# Revit family: Fireplace-Gas-Regency-Grandview_800EC
name_source: partatom
category: Mechanical Equipment
units: mm (PartAtom-declared; Revit-internal decimal feet)

## family parameters
Classification Number = 23.40.20.34.14
Cut with Voids When Loaded = Yes
Host = Face
Maintain Annotation Orientation = No
Part Type = Normal
Room Calculation Point = No
Round Connector Dimension = Use Diameter
Shared = No

## types (6) — shared parameters
Apparent Load = 0 VA
Assembly Code = D3020
C Connector Depth = 1' - 7 1/2"
C Opening Height = 2' - 7 9/16"
C Opening Width = 3' - 5"
Default Elevation = 0' - 0"
Depth = 1' - 6 7/8"
Description = G800EC Gas Fireplace
Exhaust Air Connection Diameter = 4"
Finish = Metal - Regency - Steel - Paint, Black Metallic
Frequency = 0 Hz
Glass Viewing Height = 2' - 10"
Glass Viewing Width = 3' - 0"
Height = 3' - 0 3/8"
Installation and Service URL = https://www.regency-fire.com
Keynote = 10300
Manufacturer = Regency Fireplace Products
Manufacturer Fax Number = 604-946-4349
Material = Painted Stainless Steel
Number of Poles = 1
Performance URL = https://www.regency-fire.com
Phase = 1
Product Documentation Link = https://assets.regency-fire.com
Product Name = Regency® Grandview™ G800EC Gas Fireplace
Product Page URL = https://www.regency-fire.com
Product Size = Medium
Room Size = Medium
Supply Air Connection Diameter = 7"
URL = https://www.regency-fire.com
Version = 2018 - v1.0a
Video Link = https://www.youtube.com
Voltage = 0 V
Warranty URL = https://www.regency-fire.com
Width = 2' - 11 7/8"
zero-valued in all types: Power Factor

## per-type parameters (varying)
| type | Constraints | Efficiency | EnerGuide Rating | Maximum BTU | Minimum BTU | Model |
| Cool Wall - LP | 1 | 68.16% | 57.74% | 25500.0 Btu/h | 21000.0 Btu/h | G800EC-LP |
| Clean Front - LP | 2 | 68.16% | 57.74% | 25500.0 Btu/h | 21000.0 Btu/h | G800EC-LP |
| Outside Finish - LP | 3 | 68.16% | 57.74% | 25500.0 Btu/h | 21000.0 Btu/h | G800EC-LP |
| Cool Wall - NG | 11 | 65.20% | 53.58% | 27000.0 Btu/h | 15000.0 Btu/h | G800EC-NG |
| Clean Front - NG | 22 | 65.20% | 53.58% | 27000.0 Btu/h | 15000.0 Btu/h | G800EC-NG |
| Outside Finish - NG | 33 | 65.20% | 53.58% | 27000.0 Btu/h | 15000.0 Btu/h | G800EC-NG |

## geometry (parser evidence)
native form markers: Sweep x3
no freeform markers — native parametric forms only
